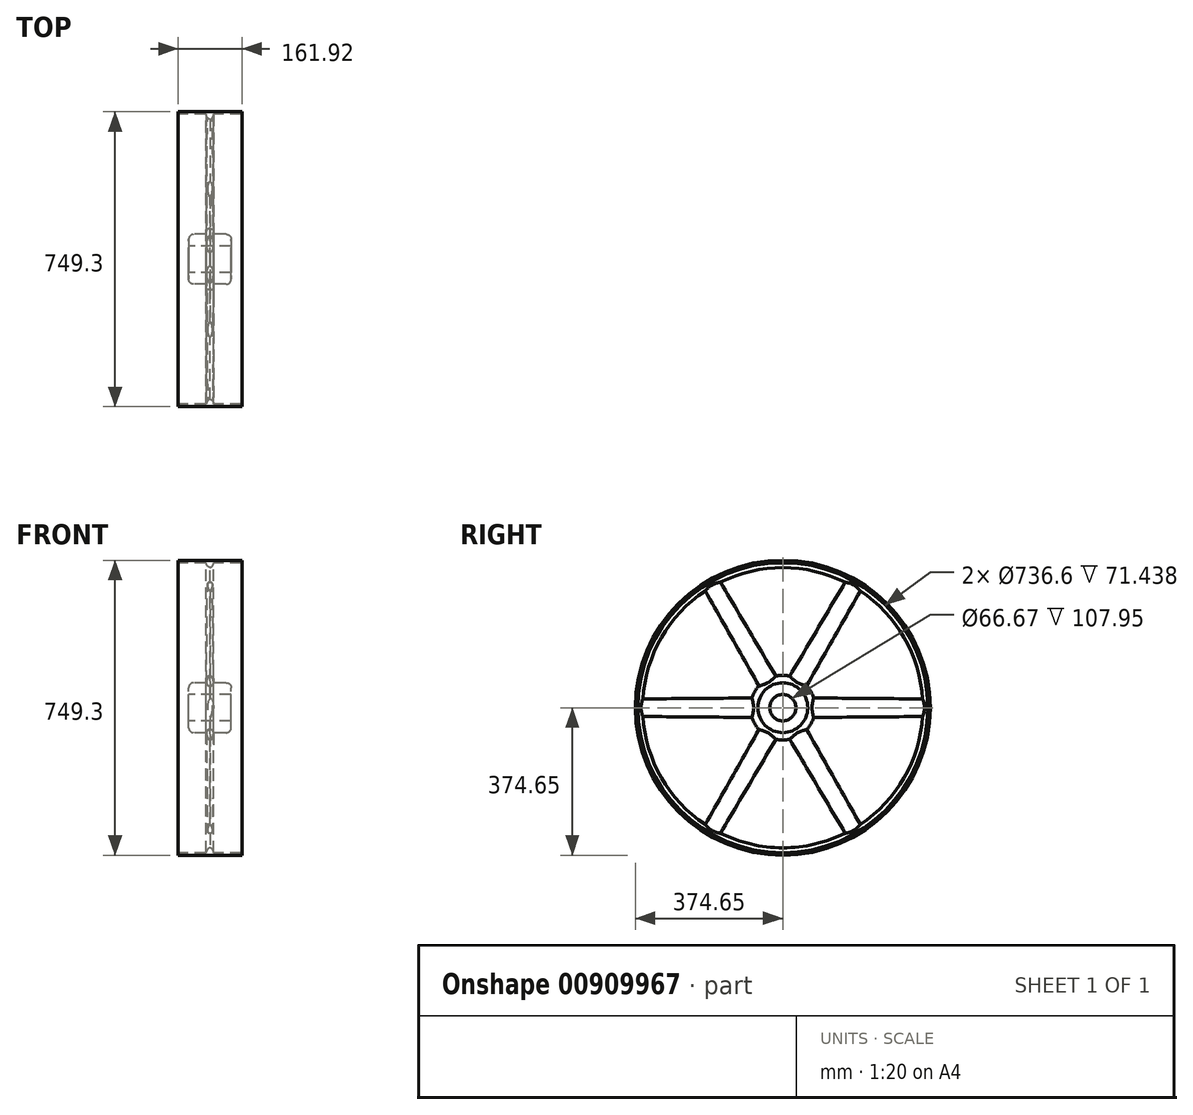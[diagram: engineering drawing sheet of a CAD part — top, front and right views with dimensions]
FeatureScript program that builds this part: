
annotation { "Feature Type Name" : "Feature", "Feature Type Description" : "" }
export const myFeature = defineFeature(function(context is Context, id is Id, definition is map)
    precondition{}
    {
        {
            var Q0;
            Q0=qCreatedBy(makeId("Front.planeOp"),FACE);
            var sketch = newSketch(context, id + "F0", { "sketchPlane" : qUnion([Q0])});
            skEllipse(sketch, "E0", {"center": v(0, 0) * mm, "majorRadius": 25.4 * mm, "minorRadius": 9.53 * mm, "majorAxis": v(0, 1)});
            skLineSegment(sketch, "E1", {"start": v(-9.53, 0) * mm, "end": v(9.53, 0) * mm, "construction": true});
            skSolve(sketch);
        }
        {
            var Q0;
            Q0=makeQuery(id+"F0.imprint","IMPRINT",FACE,{"disambiguationData":[TD([[makeQuery(id+"F0.imprint","IMPRINT",EDGE,{"derivedFrom":sQuery(id+"F0.wireOp",EDGE,"E0")}),1.0]])]});
            extrude(context, id + "F1", {"entities" : qUnion([Q0]), "depth" : 370 * mm, "offsetDistance" : 25 * mm, "hasDraft" : true, "draftAngle" : .5 * degree, "draftPullDirection" : true});
        }
        {
            var Q0;
            Q0=makeQuery(id+"F1.opExtrude","SWEPT_BODY",BODY,{"disambiguationData":[OSD([sQuery(id+"F0.wireOp",EDGE,"E0")])]});
            var Q1;
            Q1=sQuery(id+"F0.wireOp",EDGE,"E1");
            circularPattern(context, id + "F2", {"operationType" : NewBodyOperationType.ADD, "entities" : qUnion([Q0]), "axis" : qUnion([Q1]), "angle" : 360 * degree, "instanceCount" : 6, "equalSpace" : true});
        }
        {
            var Q0;
            Q0=qCreatedBy(makeId("Right.planeOp"),FACE);
            var sketch = newSketch(context, id + "F3", { "sketchPlane" : qUnion([Q0])});
            skCircle(sketch, "E2", {"center": v(0, 0) * mm, "radius": 82.55 * mm});
            skCircle(sketch, "E3", {"center": v(0, 0) * mm, "radius": 63.5 * mm});
            skCircle(sketch, "E4", {"center": v(0, 0) * mm, "radius": 33.34 * mm});
            skCircle(sketch, "E5", {"center": v(0, 0) * mm, "radius": 374.65 * mm});
            skCircle(sketch, "E6", {"center": v(0, 0) * mm, "radius": 368.3 * mm});
            skCircle(sketch, "E7", {"center": v(0, 0) * mm, "radius": 355.6 * mm});
            skSolve(sketch);
        }
        {
            var Q0;
            Q0=makeQuery(id+"F3.imprint","IMPRINT",FACE,{"disambiguationData":[TD([[makeQuery(id+"F3.imprint","IMPRINT",EDGE,{"derivedFrom":sQuery(id+"F3.wireOp",EDGE,"E3")}),1.0]])]});
            extrude(context, id + "F4", {"entities" : qUnion([Q0]), "operationType" : NewBodyOperationType.ADD, "depth" : 107.95 * mm, "offsetDistance" : 25 * mm, "symmetric" : true});
        }
        {
            var Q0;
            Q0=makeQuery(id+"F3.imprint","IMPRINT",FACE,{"disambiguationData":[TD([[makeQuery(id+"F3.imprint","IMPRINT",EDGE,{"derivedFrom":sQuery(id+"F3.wireOp",EDGE,"E2")}),1.0]])]});
            extrude(context, id + "F5", {"entities" : qUnion([Q0]), "operationType" : NewBodyOperationType.ADD, "depth" : 19.05 * mm, "offsetDistance" : 25 * mm, "symmetric" : true});
        }
        {
            var Q0;
            Q0=makeQuery(id+"F3.imprint","IMPRINT",FACE,{"disambiguationData":[TD([[makeQuery(id+"F3.imprint","IMPRINT",EDGE,{"derivedFrom":sQuery(id+"F3.wireOp",EDGE,"E4")}),1.0]])]});
            extrude(context, id + "F6", {"entities" : qUnion([Q0]), "operationType" : NewBodyOperationType.REMOVE, "oppositeDirection" : true, "depth" : 107.95 * mm, "offsetDistance" : 25 * mm, "symmetric" : true});
        }
        {
            var Q0;
            Q0=makeQuery(id+"F3.imprint","IMPRINT",FACE,{"disambiguationData":[TD([[makeQuery(id+"F3.imprint","IMPRINT",EDGE,{"derivedFrom":sQuery(id+"F3.wireOp",EDGE,"E5")}),1.0]])]});
            extrude(context, id + "F7", {"entities" : qUnion([Q0]), "operationType" : NewBodyOperationType.ADD, "depth" : 161.93 * mm, "offsetDistance" : 25 * mm, "symmetric" : true});
        }
        {
            var Q0;
            Q0=makeQuery(id+"F3.imprint","IMPRINT",FACE,{"disambiguationData":[TD([[makeQuery(id+"F3.imprint","IMPRINT",EDGE,{"derivedFrom":sQuery(id+"F3.wireOp",EDGE,"E6")}),1.0]])]});
            extrude(context, id + "F8", {"entities" : qUnion([Q0]), "operationType" : NewBodyOperationType.ADD, "depth" : 19.05 * mm, "offsetDistance" : 25 * mm, "symmetric" : true});
        }
        {
            var Q0;
            Q0=makeQuery(id+"F5.opExtrude","CAP_EDGE",EDGE,{"disambiguationData":[OSD([sQuery(id+"F3.wireOp",EDGE,"E2")])],"isStart":false});
            var Q1;
            Q1=makeQuery(id+"F5.opExtrude","CAP_EDGE",EDGE,{"disambiguationData":[OSD([sQuery(id+"F3.wireOp",EDGE,"E2")])],"isStart":true});
            var Q2;
            Q2=makeQuery(id+"F4.opExtrude","CAP_EDGE",EDGE,{"disambiguationData":[OSD([sQuery(id+"F3.wireOp",EDGE,"E3")])],"isStart":false});
            var Q3;
            Q3=makeQuery(id+"F4.opExtrude","CAP_EDGE",EDGE,{"disambiguationData":[OSD([sQuery(id+"F3.wireOp",EDGE,"E3")])],"isStart":true});
            var Q4;
            Q4=makeQuery(id+"F8.opExtrude","CAP_EDGE",EDGE,{"disambiguationData":[OSD([sQuery(id+"F3.wireOp",EDGE,"E7")])],"isStart":false});
            var Q5;
            Q5=makeQuery(id+"F8.opExtrude","CAP_EDGE",EDGE,{"disambiguationData":[OSD([sQuery(id+"F3.wireOp",EDGE,"E7")])],"isStart":true});
            fillet(context, id + "F9", {"entities" : qUnion([Q0, Q1, Q2, Q3, Q4, Q5]), "radius" : 12.7 * mm, "tangentPropagation" : true, "allowEdgeOverflow" : false});
        }
    });
